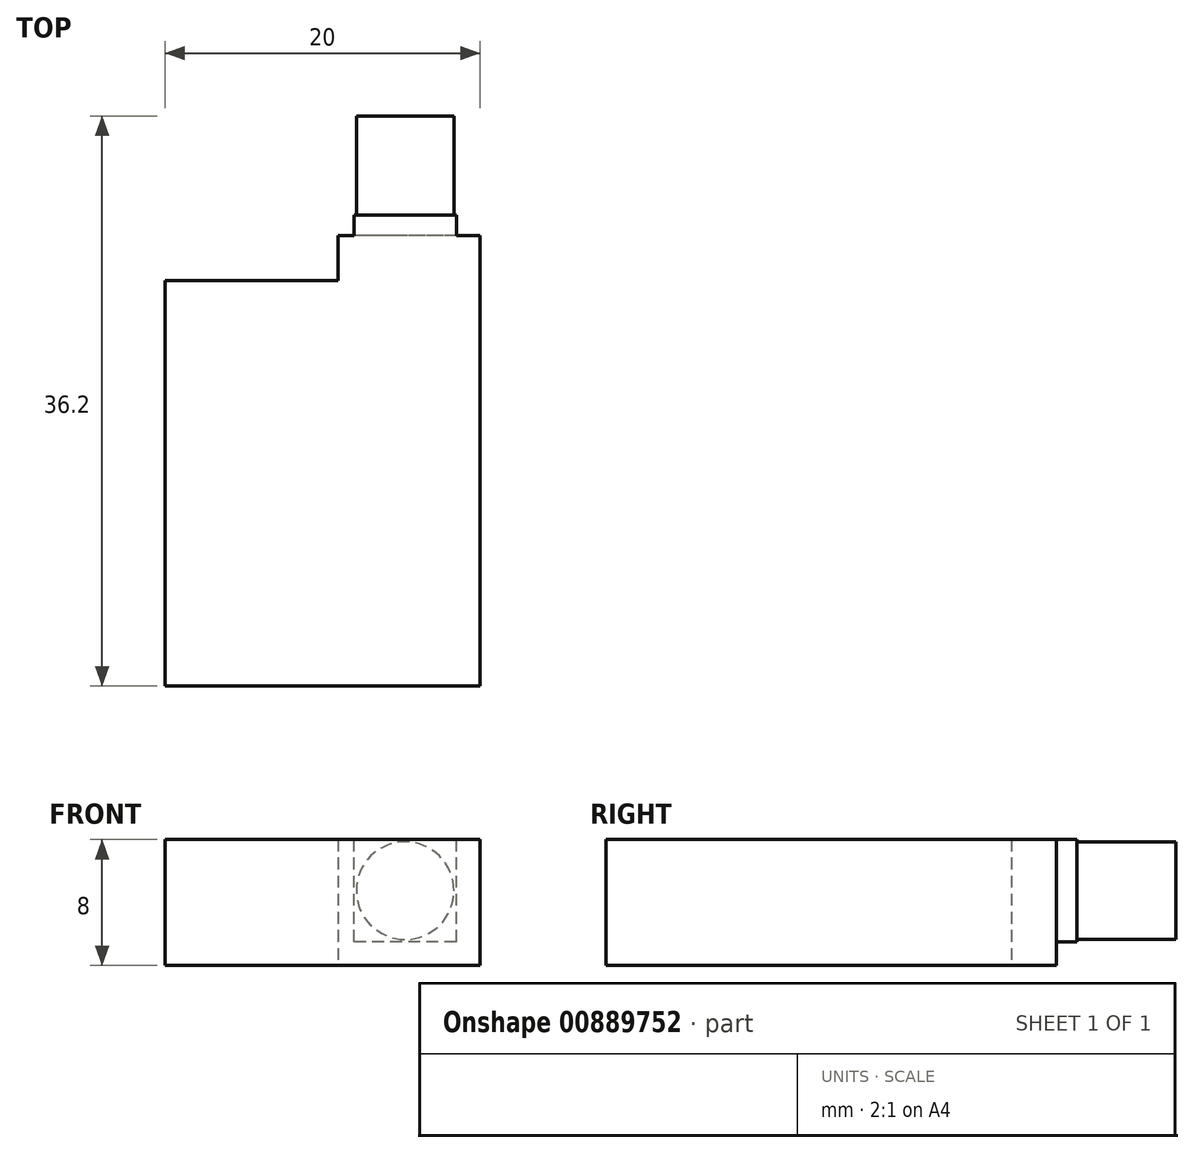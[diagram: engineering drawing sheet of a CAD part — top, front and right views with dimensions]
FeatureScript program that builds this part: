
annotation { "Feature Type Name" : "Feature", "Feature Type Description" : "" }
export const myFeature = defineFeature(function(context is Context, id is Id, definition is map)
    precondition{}
    {
        {
            var Q0;
            Q0=qCreatedBy(makeId("Top.planeOp"),FACE);
            var sketch = newSketch(context, id + "F0", { "sketchPlane" : qUnion([Q0])});
            skLineSegment(sketch, "E0.bottom", {"start": v(-11.43, 6.16) * mm, "end": v(-0.43, 6.16) * mm});
            skLineSegment(sketch, "E0.top", {"start": v(-11.43, -19.6) * mm, "end": v(8.57, -19.6) * mm});
            skLineSegment(sketch, "E0.left", {"start": v(-11.43, 6.16) * mm, "end": v(-11.43, -19.6) * mm});
            skLineSegment(sketch, "E0.right", {"start": v(8.57, 6.16) * mm, "end": v(8.57, -19.6) * mm});
            skLineSegment(sketch, "E1.top", {"start": v(8.57, 9) * mm, "end": v(-0.43, 9) * mm});
            skLineSegment(sketch, "E1.left", {"start": v(8.57, 6.16) * mm, "end": v(8.57, 9) * mm});
            skLineSegment(sketch, "E1.right", {"start": v(-0.43, 6.16) * mm, "end": v(-0.43, 9) * mm});
            skSolve(sketch);
        }
        {
            var Q0;
            Q0=makeQuery(id+"F0.imprint","IMPRINT",FACE,{"disambiguationData":[TD([[makeQuery(id+"F0.imprint","IMPRINT",EDGE,{"derivedFrom":sQuery(id+"F0.wireOp",EDGE,"E0.bottom")}),-1.0]])]});
            extrude(context, id + "F1", {"entities" : qUnion([Q0]), "depth" : 8 * mm});
        }
        {
            var Q0;
            Q0=makeQuery(id+"F1.opExtrude","SWEPT_FACE",FACE,{"disambiguationData":[OSD([sQuery(id+"F0.wireOp",EDGE,"E1.top")])]});
            var sketch = newSketch(context, id + "F2", { "sketchPlane" : qUnion([Q0])});
            skLineSegment(sketch, "E2.bottom", {"start": v(-7.07, 1.5) * mm, "end": v(-0.57, 1.5) * mm});
            skLineSegment(sketch, "E2.top", {"start": v(-7.07, 8) * mm, "end": v(-0.57, 8) * mm});
            skLineSegment(sketch, "E2.left", {"start": v(-7.07, 1.5) * mm, "end": v(-7.07, 8) * mm});
            skLineSegment(sketch, "E2.right", {"start": v(-0.57, 1.5) * mm, "end": v(-0.57, 8) * mm});
            skSolve(sketch);
        }
        {
            var Q0;
            Q0=makeQuery(id+"F2.imprint","IMPRINT",FACE,{"disambiguationData":[TD([[makeQuery(id+"F2.imprint","IMPRINT",EDGE,{"derivedFrom":sQuery(id+"F2.wireOp",EDGE,"E2.bottom")}),1.0]])]});
            extrude(context, id + "F3", {"entities" : qUnion([Q0]), "operationType" : NewBodyOperationType.ADD, "depth" : 1.3 * mm});
        }
        {
            var Q0;
            Q0=makeQuery(id+"F3.opExtrude","CAP_FACE",FACE,{"disambiguationData":[OSD([sQuery(id+"F2.wireOp",EDGE,"E2.bottom"),sQuery(id+"F2.wireOp",EDGE,"E2.top"),sQuery(id+"F2.wireOp",EDGE,"E2.left"),sQuery(id+"F2.wireOp",EDGE,"E2.right")])],"isStart":false});
            var sketch = newSketch(context, id + "F4", { "sketchPlane" : qUnion([Q0])});
            skCircle(sketch, "E3", {"center": v(-3.82, 4.75) * mm, "radius": 3.1 * mm});
            skLineSegment(sketch, "E4", {"start": v(-7.07, 1.5) * mm, "end": v(-0.57, 8) * mm, "construction": true});
            skSolve(sketch);
        }
        {
            var Q0;
            Q0=qSketchRegion(id+"F4",true);
            extrude(context, id + "F5", {"entities" : qUnion([Q0]), "operationType" : NewBodyOperationType.ADD, "depth" : 6.3 * mm});
        }
    });
